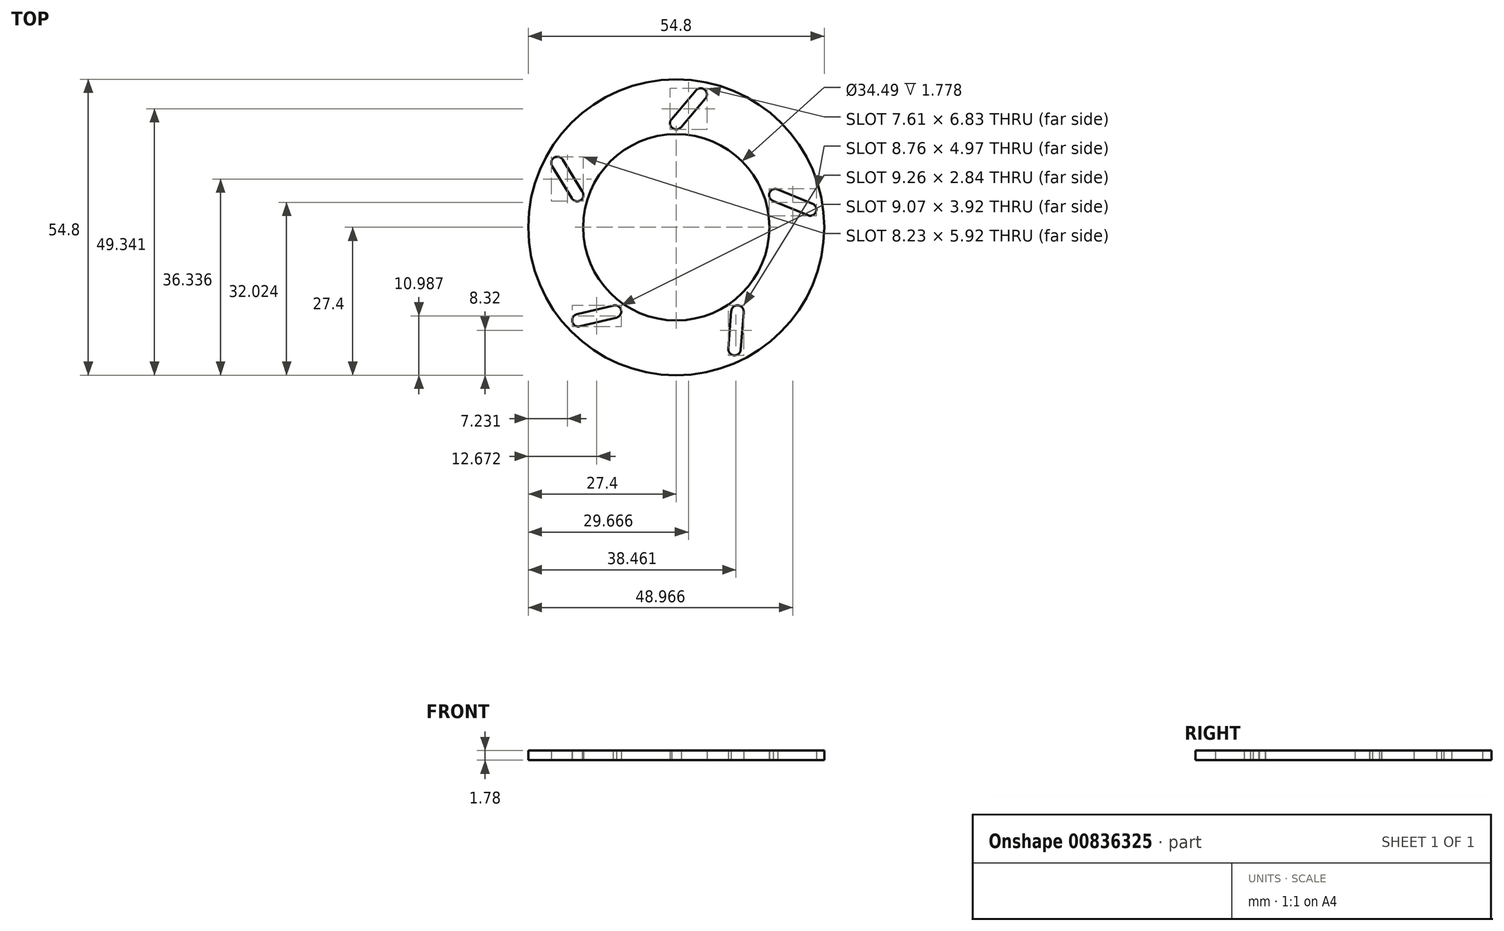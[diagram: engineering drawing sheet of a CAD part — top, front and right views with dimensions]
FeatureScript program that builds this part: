
annotation { "Feature Type Name" : "Feature", "Feature Type Description" : "" }
export const myFeature = defineFeature(function(context is Context, id is Id, definition is map)
    precondition{}
    {
        {
            var Q0;
            Q0=qCreatedBy(makeId("Top.planeOp"),FACE);
            var sketch = newSketch(context, id + "F0", { "sketchPlane" : qUnion([Q0])});
            skCircle(sketch, "E0", {"center": v(0, 0) * mm, "radius": 27.4 * mm});
            skSolve(sketch);
        }
        {
            var Q0;
            Q0=qCreatedBy(makeId("Top.planeOp"),FACE);
            var sketch = newSketch(context, id + "F1", { "sketchPlane" : qUnion([Q0])});
            skCircle(sketch, "E1", {"center": v(0, 0) * mm, "radius": 17.25 * mm});
            skSolve(sketch);
        }
        {
            var Q0;
            Q0=qSketchRegion(id+"F0",true);
            extrude(context, id + "F2", {"entities" : qUnion([Q0]), "depth" : 1.78 * mm, "offsetDistance" : 25.4 * mm});
        }
        {
            var Q0;
            Q0=qSketchRegion(id+"F1",true);
            extrude(context, id + "F3", {"entities" : qUnion([Q0]), "operationType" : NewBodyOperationType.REMOVE, "endBound" : BoundingType.UP_TO_NEXT, "depth" : 25.4 * mm, "offsetDistance" : 25.4 * mm});
        }
        {
            var Q0;
            Q0=qCreatedBy(makeId("Front.planeOp"),FACE);
            var sketch = newSketch(context, id + "F4", { "sketchPlane" : qUnion([Q0])});
            skLineSegment(sketch, "E2", {"start": v(0, 77.2) * mm, "end": v(0, -74.83) * mm});
            skSolve(sketch);
        }
        {
            var Q0;
            Q0=qCreatedBy(makeId("Top.planeOp"),FACE);
            var sketch = newSketch(context, id + "F5", { "sketchPlane" : qUnion([Q0])});
            skArc(sketch, "E3", {"start": v(-0.86, 20.04) * mm, "mid": v(-0.73, 18.39) * mm, "end": v(0.92, 18.59) * mm});
            skArc(sketch, "E4", {"start": v(5.4, 23.85) * mm, "mid": v(5.28, 25.47) * mm, "end": v(3.66, 25.34) * mm});
            skLineSegment(sketch, "E5", {"start": v(-0.89, 20.01) * mm, "end": v(3.66, 25.34) * mm});
            skLineSegment(sketch, "E6", {"start": v(0.83, 18.48) * mm, "end": v(5.4, 23.85) * mm});
            skSolve(sketch);
        }
        {
            var Q0;
            Q0 = qSketchRegion(id + "F5", true);
            extrude(context, id + "F6", {"entities" : qUnion([Q0]), "endBound" : BoundingType.UP_TO_NEXT, "depth" : 25.4 * mm, "offsetDistance" : 25.4 * mm});
        }
        {
            var Q0;
            Q0=makeQuery(id+"F6.opExtrude","SWEPT_BODY",BODY,{"disambiguationData":[OSD([sQuery(id+"F5.wireOp",EDGE,"E3"),sQuery(id+"F5.wireOp",EDGE,"E4"),sQuery(id+"F5.wireOp",EDGE,"E5"),sQuery(id+"F5.wireOp",EDGE,"E6")])]});
            var Q1;
            Q1=sQuery(id+"F4.wireOp",EDGE,"E2");
            circularPattern(context, id + "F7", {"entities" : qUnion([Q0]), "axis" : qUnion([Q1]), "angle" : 360 * degree, "instanceCount" : 5, "equalSpace" : true});
        }
        {
            var Q0;
            Q0=makeQuery(id+"F6.opExtrude","SWEPT_BODY",BODY,{"disambiguationData":[OSD([sQuery(id+"F5.wireOp",EDGE,"E3"),sQuery(id+"F5.wireOp",EDGE,"E4"),sQuery(id+"F5.wireOp",EDGE,"E5"),sQuery(id+"F5.wireOp",EDGE,"E6")])]});
            var Q1;
            Q1=makeQuery(id+"F7.opPattern","COPY",BODY,{"derivedFrom":makeQuery(id+"F6.opExtrude","SWEPT_BODY",BODY,{"disambiguationData":[OSD([sQuery(id+"F5.wireOp",EDGE,"E3"),sQuery(id+"F5.wireOp",EDGE,"E4"),sQuery(id+"F5.wireOp",EDGE,"E5"),sQuery(id+"F5.wireOp",EDGE,"E6")])]}),"instanceName":"1"});
            var Q2;
            Q2=makeQuery(id+"F7.opPattern","COPY",BODY,{"derivedFrom":makeQuery(id+"F6.opExtrude","SWEPT_BODY",BODY,{"disambiguationData":[OSD([sQuery(id+"F5.wireOp",EDGE,"E3"),sQuery(id+"F5.wireOp",EDGE,"E4"),sQuery(id+"F5.wireOp",EDGE,"E5"),sQuery(id+"F5.wireOp",EDGE,"E6")])]}),"instanceName":"2"});
            var Q3;
            Q3=makeQuery(id+"F7.opPattern","COPY",BODY,{"derivedFrom":makeQuery(id+"F6.opExtrude","SWEPT_BODY",BODY,{"disambiguationData":[OSD([sQuery(id+"F5.wireOp",EDGE,"E3"),sQuery(id+"F5.wireOp",EDGE,"E4"),sQuery(id+"F5.wireOp",EDGE,"E5"),sQuery(id+"F5.wireOp",EDGE,"E6")])]}),"instanceName":"3"});
            var Q4;
            Q4=makeQuery(id+"F7.opPattern","COPY",BODY,{"derivedFrom":makeQuery(id+"F6.opExtrude","SWEPT_BODY",BODY,{"disambiguationData":[OSD([sQuery(id+"F5.wireOp",EDGE,"E3"),sQuery(id+"F5.wireOp",EDGE,"E4"),sQuery(id+"F5.wireOp",EDGE,"E5"),sQuery(id+"F5.wireOp",EDGE,"E6")])]}),"instanceName":"4"});
            var Q5;
            Q5=makeQuery(id+"F2.opExtrude","SWEPT_BODY",BODY,{"disambiguationData":[OSD([sQuery(id+"F0.wireOp",EDGE,"E0")])]});
            booleanBodies(context, id + "F8", {"operationType" : BooleanOperationType.SUBTRACTION, "tools" : qUnion([Q0, Q1, Q2, Q3, Q4]), "targets" : qUnion([Q5])});
        }
    });
